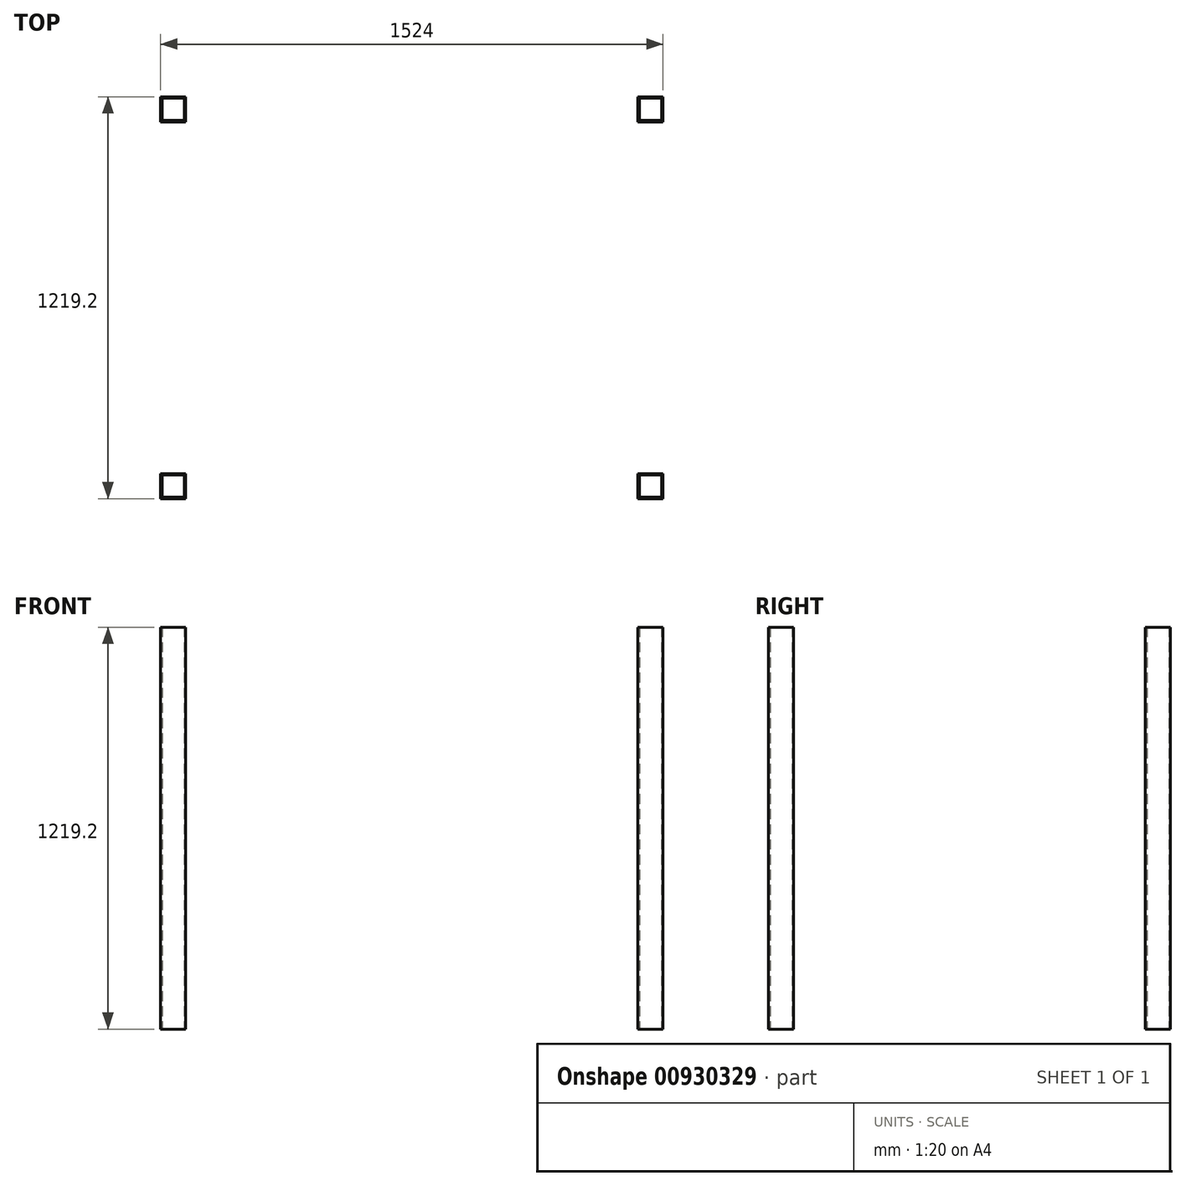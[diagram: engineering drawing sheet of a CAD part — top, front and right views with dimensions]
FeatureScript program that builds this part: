
annotation { "Feature Type Name" : "Feature", "Feature Type Description" : "" }
export const myFeature = defineFeature(function(context is Context, id is Id, definition is map)
    precondition{}
    {
        {
            var Q0;
            Q0=qCreatedBy(makeId("Top.planeOp"),FACE);
            var sketch = newSketch(context, id + "F0", { "sketchPlane" : qUnion([Q0])});
            skLineSegment(sketch, "E0.bottom", {"start": v(-693.95, 744.3) * mm, "end": v(-617.75, 744.3) * mm});
            skLineSegment(sketch, "E0.top", {"start": v(-693.95, 668.1) * mm, "end": v(-617.75, 668.1) * mm});
            skLineSegment(sketch, "E0.left", {"start": v(-693.95, 744.3) * mm, "end": v(-693.95, 668.1) * mm});
            skLineSegment(sketch, "E0.right", {"start": v(-617.75, 744.3) * mm, "end": v(-617.75, 668.1) * mm});
            skLineSegment(sketch, "E1.bottom", {"start": v(753.85, 744.3) * mm, "end": v(830.05, 744.3) * mm});
            skLineSegment(sketch, "E1.top", {"start": v(753.85, 668.1) * mm, "end": v(830.05, 668.1) * mm});
            skLineSegment(sketch, "E1.left", {"start": v(753.85, 744.3) * mm, "end": v(753.85, 668.1) * mm});
            skLineSegment(sketch, "E1.right", {"start": v(830.05, 744.3) * mm, "end": v(830.05, 668.1) * mm});
            skLineSegment(sketch, "E2.bottom", {"start": v(-693.95, -398.7) * mm, "end": v(-617.75, -398.7) * mm});
            skLineSegment(sketch, "E2.top", {"start": v(-693.95, -474.9) * mm, "end": v(-617.75, -474.9) * mm});
            skLineSegment(sketch, "E2.left", {"start": v(-693.95, -398.7) * mm, "end": v(-693.95, -474.9) * mm});
            skLineSegment(sketch, "E2.right", {"start": v(-617.75, -398.7) * mm, "end": v(-617.75, -474.9) * mm});
            skLineSegment(sketch, "E3.bottom", {"start": v(753.85, -398.7) * mm, "end": v(830.05, -398.7) * mm});
            skLineSegment(sketch, "E3.top", {"start": v(753.85, -474.9) * mm, "end": v(830.05, -474.9) * mm});
            skLineSegment(sketch, "E3.left", {"start": v(753.85, -398.7) * mm, "end": v(753.85, -474.9) * mm});
            skLineSegment(sketch, "E3.right", {"start": v(830.05, -398.7) * mm, "end": v(830.05, -474.9) * mm});
            skLineSegment(sketch, "E4.bottom", {"start": v(-689.98, 740.32) * mm, "end": v(-621.72, 740.32) * mm});
            skLineSegment(sketch, "E4.top", {"start": v(-689.98, 672.06) * mm, "end": v(-621.72, 672.06) * mm});
            skLineSegment(sketch, "E4.left", {"start": v(-689.98, 740.32) * mm, "end": v(-689.98, 672.06) * mm});
            skLineSegment(sketch, "E4.right", {"start": v(-621.72, 740.32) * mm, "end": v(-621.72, 672.06) * mm});
            skLineSegment(sketch, "E5.bottom", {"start": v(-689.98, -402.68) * mm, "end": v(-621.72, -402.68) * mm});
            skLineSegment(sketch, "E5.top", {"start": v(-689.98, -470.94) * mm, "end": v(-621.72, -470.94) * mm});
            skLineSegment(sketch, "E5.left", {"start": v(-689.98, -402.68) * mm, "end": v(-689.98, -470.94) * mm});
            skLineSegment(sketch, "E5.right", {"start": v(-621.72, -402.68) * mm, "end": v(-621.72, -470.94) * mm});
            skLineSegment(sketch, "E6.bottom", {"start": v(757.82, -402.68) * mm, "end": v(826.08, -402.68) * mm});
            skLineSegment(sketch, "E6.top", {"start": v(757.82, -470.94) * mm, "end": v(826.08, -470.94) * mm});
            skLineSegment(sketch, "E6.left", {"start": v(757.82, -402.68) * mm, "end": v(757.82, -470.94) * mm});
            skLineSegment(sketch, "E6.right", {"start": v(826.08, -402.68) * mm, "end": v(826.08, -470.94) * mm});
            skLineSegment(sketch, "E7.bottom", {"start": v(757.82, 740.32) * mm, "end": v(826.08, 740.32) * mm});
            skLineSegment(sketch, "E7.top", {"start": v(757.82, 672.06) * mm, "end": v(826.08, 672.06) * mm});
            skLineSegment(sketch, "E7.left", {"start": v(757.82, 740.32) * mm, "end": v(757.82, 672.06) * mm});
            skLineSegment(sketch, "E7.right", {"start": v(826.08, 740.32) * mm, "end": v(826.08, 672.06) * mm});
            skSolve(sketch);
        }
        {
            var Q0;
            Q0 = qSketchRegion(id + "F0", true);
            extrude(context, id + "F1", {"entities" : qUnion([Q0]), "depth" : 1219.2 * mm, "offsetDistance" : 25.4 * mm});
        }
    });
